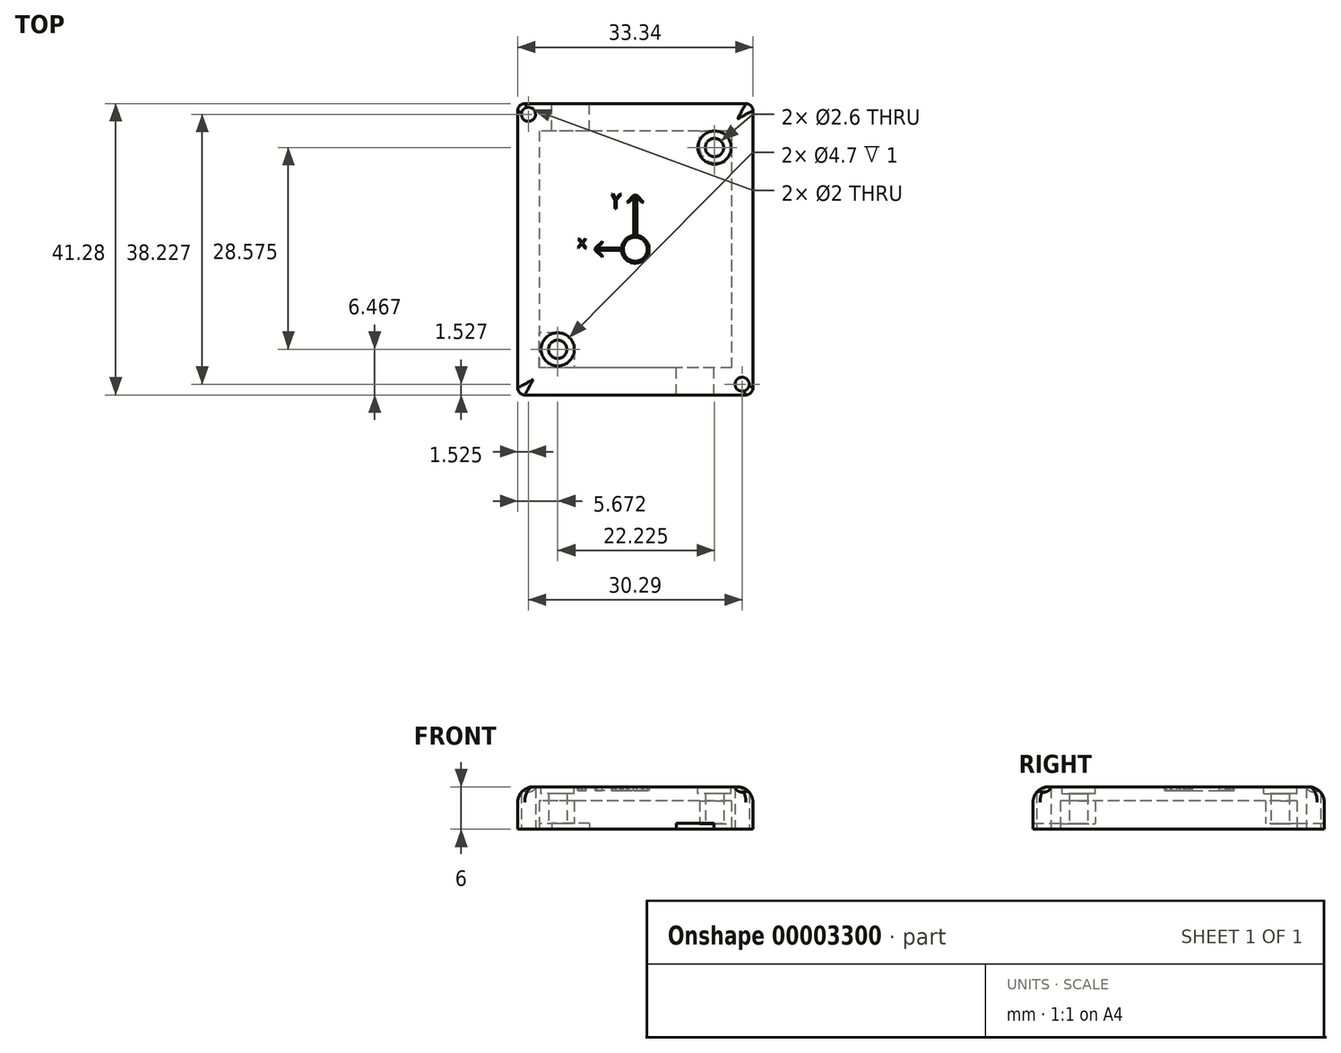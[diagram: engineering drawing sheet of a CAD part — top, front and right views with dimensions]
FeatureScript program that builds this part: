
annotation { "Feature Type Name" : "Feature", "Feature Type Description" : "" }
export const myFeature = defineFeature(function(context is Context, id is Id, definition is map)
    precondition{}
    {
        {
            var Q0;
            Q0=qCreatedBy(makeId("Top.planeOp"),FACE);
            var sketch = newSketch(context, id + "F0", { "sketchPlane" : qUnion([Q0])});
            skLineSegment(sketch, "E0.rect.bottom", {"start": v(16.67, 20.64) * mm, "end": v(-16.67, 20.64) * mm});
            skLineSegment(sketch, "E0.rect.top", {"start": v(16.67, -20.64) * mm, "end": v(-16.67, -20.64) * mm});
            skLineSegment(sketch, "E0.rect.left", {"start": v(16.67, 20.64) * mm, "end": v(16.67, -20.64) * mm});
            skLineSegment(sketch, "E0.rect.right", {"start": v(-16.67, 20.64) * mm, "end": v(-16.67, -20.64) * mm});
            skPoint(sketch, "E0.rect.middle", {"position": v(0, 0) * mm});
            skSolve(sketch);
        }
        {
            var Q0;
            Q0=makeQuery(id+"F0.imprint","IMPRINT",FACE,{"disambiguationData":[TD([[makeQuery(id+"F0.imprint","IMPRINT",EDGE,{"derivedFrom":sQuery(id+"F0.wireOp",EDGE,"E0.rect.bottom")}),1.0]])]});
            extrude(context, id + "F1", {"entities" : qUnion([Q0]), "oppositeDirection" : true, "depth" : 6 * mm});
        }
        {
            var Q0;
            Q0=makeQuery(id+"F1.opExtrude","CAP_FACE",FACE,{"disambiguationData":[OSD([sQuery(id+"F0.wireOp",EDGE,"E0.rect.bottom"),sQuery(id+"F0.wireOp",EDGE,"E0.rect.top"),sQuery(id+"F0.wireOp",EDGE,"E0.rect.left"),sQuery(id+"F0.wireOp",EDGE,"E0.rect.right")])],"isStart":true});
            var sketch = newSketch(context, id + "F2", { "sketchPlane" : qUnion([Q0])});
            skLineSegment(sketch, "E1.rect.bottom", {"start": v(13.33, 16.51) * mm, "end": v(-13.34, 16.51) * mm});
            skLineSegment(sketch, "E1.rect.top", {"start": v(13.34, -16.51) * mm, "end": v(-13.33, -16.51) * mm});
            skLineSegment(sketch, "E1.rect.left", {"start": v(13.33, 16.51) * mm, "end": v(13.34, -16.51) * mm});
            skLineSegment(sketch, "E1.rect.right", {"start": v(-13.34, 16.51) * mm, "end": v(-13.33, -16.51) * mm});
            skPoint(sketch, "E1.rect.middle", {"position": v(0, 0) * mm});
            skCircle(sketch, "E2", {"center": v(11.23, 14.4) * mm, "radius": 1.25 * mm});
            skCircle(sketch, "E3", {"center": v(-11, -14.17) * mm, "radius": 1.25 * mm});
            skCircle(sketch, "E4", {"center": v(11.23, 14.4) * mm, "radius": 2.1 * mm});
            skCircle(sketch, "E5", {"center": v(-11, -14.17) * mm, "radius": 2.34 * mm});
            skLineSegment(sketch, "E6.0", {"start": v(13.59, 16.76) * mm, "end": v(-13.59, 16.76) * mm});
            skLineSegment(sketch, "E6.1", {"start": v(13.59, 16.76) * mm, "end": v(13.59, -16.76) * mm});
            skLineSegment(sketch, "E6.2", {"start": v(13.59, -16.76) * mm, "end": v(-13.59, -16.76) * mm});
            skLineSegment(sketch, "E6.3", {"start": v(-13.59, 16.76) * mm, "end": v(-13.59, -16.76) * mm});
            skLineSegment(sketch, "E7", {"start": v(9.12, 14.4) * mm, "end": v(9.12, 16.76) * mm});
            skLineSegment(sketch, "E8", {"start": v(11.23, 12.3) * mm, "end": v(13.59, 12.3) * mm});
            skLineSegment(sketch, "E9", {"start": v(-11, -11.84) * mm, "end": v(-13.59, -11.84) * mm});
            skLineSegment(sketch, "E10", {"start": v(-8.66, -14.17) * mm, "end": v(-8.66, -16.76) * mm});
            skSolve(sketch);
        }
        {
            var Q0;
            {var subQ6=sQuery(id+"F2.wireOp",EDGE,"E1.rect.right");var subQ10=sQuery(id+"F2.wireOp",EDGE,"E1.rect.bottom");var subQ18=makeQuery(id+"F2.imprint","INTERSECT",VERTEX,{"derivedFrom":[subQ10,subQ6]});Q0=makeQuery(id+"F2.imprint","IMPRINT",FACE,{"disambiguationData":[TD([[makeQuery(id+"F2.imprint","IMPRINT",EDGE,{"disambiguationData":[TD([[subQ18,1.0]])],"derivedFrom":subQ10}),1.0]])]});}
            var Q1;
            {var subQ1=sQuery(id+"F2.wireOp",EDGE,"E1.rect.right");var subQ6=sQuery(id+"F2.wireOp",EDGE,"E1.rect.bottom");var subQ11=makeQuery(id+"F2.imprint","INTERSECT",VERTEX,{"derivedFrom":[subQ6,subQ1]});Q1=makeQuery(id+"F2.imprint","IMPRINT",FACE,{"disambiguationData":[TD([[makeQuery(id+"F2.imprint","IMPRINT",EDGE,{"disambiguationData":[TD([[subQ11,1.0]])],"derivedFrom":subQ6}),-1.0]])]});}
            var Q2;
            {var subQ1=sQuery(id+"F2.wireOp",EDGE,"E1.rect.left");var subQ6=sQuery(id+"F2.wireOp",EDGE,"E1.rect.top");var subQ11=makeQuery(id+"F2.imprint","INTERSECT",VERTEX,{"derivedFrom":[subQ6,subQ1]});Q2=makeQuery(id+"F2.imprint","IMPRINT",FACE,{"disambiguationData":[TD([[makeQuery(id+"F2.imprint","IMPRINT",EDGE,{"disambiguationData":[TD([[subQ11,-1.0]])],"derivedFrom":subQ6}),1.0]])]});}
            extrude(context, id + "F3", {"entities" : qUnion([Q0, Q1, Q2]), "operationType" : NewBodyOperationType.REMOVE, "oppositeDirection" : true, "depth" : 4 * mm});
        }
        {
            var Q0;
            Q0=makeQuery(id+"F1.opExtrude","CAP_FACE",FACE,{"disambiguationData":[OSD([sQuery(id+"F0.wireOp",EDGE,"E0.rect.bottom"),sQuery(id+"F0.wireOp",EDGE,"E0.rect.top"),sQuery(id+"F0.wireOp",EDGE,"E0.rect.left"),sQuery(id+"F0.wireOp",EDGE,"E0.rect.right")])],"isStart":true});
            var sketch = newSketch(context, id + "F4", { "sketchPlane" : qUnion([Q0])});
            skLineSegment(sketch, "E11", {"start": v(9.12, 16.76) * mm, "end": v(13.59, 16.76) * mm});
            skLineSegment(sketch, "E12", {"start": v(13.59, 16.76) * mm, "end": v(13.59, 12.3) * mm});
            skLineSegment(sketch, "E13", {"start": v(13.59, 12.3) * mm, "end": v(11.23, 12.3) * mm});
            skArc(sketch, "E14", {"start": v(9.12, 14.4) * mm, "mid": v(9.74, 12.91) * mm, "end": v(11.23, 12.3) * mm});
            skLineSegment(sketch, "E15", {"start": v(9.12, 14.4) * mm, "end": v(9.12, 16.76) * mm});
            skArc(sketch, "E16", {"start": v(-8.66, -14.17) * mm, "mid": v(-9.35, -12.52) * mm, "end": v(-11, -11.84) * mm});
            skLineSegment(sketch, "E17", {"start": v(-8.66, -14.17) * mm, "end": v(-8.66, -16.76) * mm});
            skLineSegment(sketch, "E18", {"start": v(-8.66, -16.76) * mm, "end": v(-13.59, -16.76) * mm});
            skLineSegment(sketch, "E19", {"start": v(-13.59, -16.76) * mm, "end": v(-13.59, -11.84) * mm});
            skLineSegment(sketch, "E20", {"start": v(-13.59, -11.84) * mm, "end": v(-11, -11.84) * mm});
            skSolve(sketch);
        }
        {
            var Q0;
            {Q0=qUnion([makeQuery(id+"F4.imprint","IMPRINT",FACE,{"disambiguationData":[TD([[makeQuery(id+"F4.imprint","IMPRINT",EDGE,{"derivedFrom":sQuery(id+"F4.wireOp",EDGE,"E11")}),-1.0]])]}),makeQuery(id+"F4.imprint","IMPRINT",FACE,{"disambiguationData":[TD([[makeQuery(id+"F4.imprint","IMPRINT",EDGE,{"derivedFrom":sQuery(id+"F4.wireOp",EDGE,"E16")}),1.0]])]})]);}
            extrude(context, id + "F5", {"entities" : qUnion([Q0]), "operationType" : NewBodyOperationType.REMOVE, "oppositeDirection" : true, "depth" : .8 * mm});
        }
        {
            var Q0;
            Q0=makeQuery(id+"F5.boolean.opBoolean","COPY",FACE,{"derivedFrom":makeQuery(id+"F5.opExtrude","CAP_FACE",FACE,{"disambiguationData":[OSD([sQuery(id+"F4.wireOp",EDGE,"E11"),sQuery(id+"F4.wireOp",EDGE,"E12"),sQuery(id+"F4.wireOp",EDGE,"E13"),sQuery(id+"F4.wireOp",EDGE,"E14"),sQuery(id+"F4.wireOp",EDGE,"E15")])],"isStart":false})});
            var sketch = newSketch(context, id + "F6", { "sketchPlane" : qUnion([Q0])});
            skCircle(sketch, "E21", {"center": v(11.23, 14.4) * mm, "radius": 1.3 * mm});
            skSolve(sketch);
        }
        {
            var Q0;
            Q0=makeQuery(id+"F6.imprint","IMPRINT",FACE,{"disambiguationData":[TD([[makeQuery(id+"F6.imprint","IMPRINT",EDGE,{"derivedFrom":sQuery(id+"F6.wireOp",EDGE,"E21")}),1.0]])]});
            extrude(context, id + "F7", {"entities" : qUnion([Q0]), "operationType" : NewBodyOperationType.REMOVE, "oppositeDirection" : true, "depth" : 25.4 * mm});
        }
        {
            var Q0;
            Q0=makeQuery(id+"F5.boolean.opBoolean","COPY",FACE,{"derivedFrom":makeQuery(id+"F5.opExtrude","CAP_FACE",FACE,{"disambiguationData":[OSD([sQuery(id+"F4.wireOp",EDGE,"E16"),sQuery(id+"F4.wireOp",EDGE,"E17"),sQuery(id+"F4.wireOp",EDGE,"E18"),sQuery(id+"F4.wireOp",EDGE,"E19"),sQuery(id+"F4.wireOp",EDGE,"E20")])],"isStart":false})});
            var sketch = newSketch(context, id + "F8", { "sketchPlane" : qUnion([Q0])});
            skCircle(sketch, "E22", {"center": v(-11, -14.17) * mm, "radius": 1.3 * mm});
            skSolve(sketch);
        }
        {
            var Q0;
            Q0=makeQuery(id+"F8.imprint","IMPRINT",FACE,{"disambiguationData":[TD([[makeQuery(id+"F8.imprint","IMPRINT",EDGE,{"derivedFrom":sQuery(id+"F8.wireOp",EDGE,"E22")}),1.0]])]});
            extrude(context, id + "F9", {"entities" : qUnion([Q0]), "operationType" : NewBodyOperationType.REMOVE, "oppositeDirection" : true, "depth" : 25.4 * mm});
        }
        {
            var Q0;
            Q0=makeQuery(id+"F1.opExtrude","CAP_FACE",FACE,{"disambiguationData":[OSD([sQuery(id+"F0.wireOp",EDGE,"E0.rect.bottom"),sQuery(id+"F0.wireOp",EDGE,"E0.rect.top"),sQuery(id+"F0.wireOp",EDGE,"E0.rect.left"),sQuery(id+"F0.wireOp",EDGE,"E0.rect.right")])],"isStart":true});
            var sketch = newSketch(context, id + "F10", { "sketchPlane" : qUnion([Q0])});
            skLineSegment(sketch, "E23.bottom", {"start": v(-13.59, 16.76) * mm, "end": v(-5.09, 16.76) * mm});
            skLineSegment(sketch, "E23.top", {"start": v(-13.59, 20.64) * mm, "end": v(-5.09, 20.64) * mm});
            skLineSegment(sketch, "E23.left", {"start": v(-13.59, 16.76) * mm, "end": v(-13.59, 20.64) * mm});
            skLineSegment(sketch, "E23.right", {"start": v(-5.09, 16.76) * mm, "end": v(-5.09, 20.64) * mm});
            skLineSegment(sketch, "E24.bottom", {"start": v(13.59, -16.76) * mm, "end": v(4.59, -16.76) * mm});
            skLineSegment(sketch, "E24.top", {"start": v(13.59, -20.64) * mm, "end": v(4.59, -20.64) * mm});
            skLineSegment(sketch, "E24.left", {"start": v(13.59, -16.76) * mm, "end": v(13.59, -20.64) * mm});
            skLineSegment(sketch, "E24.right", {"start": v(4.59, -16.76) * mm, "end": v(4.59, -20.64) * mm});
            skSolve(sketch);
        }
        {
            var Q0;
            {Q0=qUnion([makeQuery(id+"F10.imprint","IMPRINT",FACE,{"disambiguationData":[TD([[makeQuery(id+"F10.imprint","IMPRINT",EDGE,{"derivedFrom":sQuery(id+"F10.wireOp",EDGE,"E23.bottom")}),-1.0]])]}),makeQuery(id+"F10.imprint","IMPRINT",FACE,{"disambiguationData":[TD([[makeQuery(id+"F10.imprint","IMPRINT",EDGE,{"derivedFrom":sQuery(id+"F10.wireOp",EDGE,"E24.bottom")}),1.0]])]})]);}
            extrude(context, id + "F11", {"entities" : qUnion([Q0]), "operationType" : NewBodyOperationType.REMOVE, "oppositeDirection" : true, "depth" : .4 * mm});
        }
        {
            var Q0;
            Q0=makeQuery(id+"F1.opExtrude","SWEPT_BODY",BODY,{"disambiguationData":[OSD([sQuery(id+"F0.wireOp",EDGE,"E0.rect.bottom"),sQuery(id+"F0.wireOp",EDGE,"E0.rect.top"),sQuery(id+"F0.wireOp",EDGE,"E0.rect.left"),sQuery(id+"F0.wireOp",EDGE,"E0.rect.right")])]});
            var Q1;
            Q1=qCreatedBy(makeId("Top.planeOp"),FACE);
            mirror(context, id + "F12", {"entities" : qUnion([Q0]), "mirrorPlane" : qUnion([Q1])});
        }
        {
            var Q0;
            Q0=makeQuery(id+"F1.opExtrude","SWEPT_BODY",BODY,{"disambiguationData":[OSD([sQuery(id+"F0.wireOp",EDGE,"E0.rect.bottom"),sQuery(id+"F0.wireOp",EDGE,"E0.rect.top"),sQuery(id+"F0.wireOp",EDGE,"E0.rect.left"),sQuery(id+"F0.wireOp",EDGE,"E0.rect.right")])]});
            deleteBodies(context, id + "F13", {"entities" : qUnion([Q0])});
        }
        {
            var Q0;
            Q0=makeQuery(id+"F12.opPattern","COPY",FACE,{"derivedFrom":makeQuery(id+"F1.opExtrude","CAP_FACE",FACE,{"disambiguationData":[OSD([sQuery(id+"F0.wireOp",EDGE,"E0.rect.bottom"),sQuery(id+"F0.wireOp",EDGE,"E0.rect.top"),sQuery(id+"F0.wireOp",EDGE,"E0.rect.left"),sQuery(id+"F0.wireOp",EDGE,"E0.rect.right")])],"isStart":false}),"instanceName":"1"});
            var sketch = newSketch(context, id + "F14", { "sketchPlane" : qUnion([Q0])});
            skCircle(sketch, "E25", {"center": v(11.23, 14.4) * mm, "radius": 2.35 * mm});
            skCircle(sketch, "E26", {"center": v(-11, -14.17) * mm, "radius": 2.35 * mm});
            skSolve(sketch);
        }
        {
            var Q0;
            {var subQ0=makeQuery(id+"F1.opExtrude","CAP_FACE",FACE,{"disambiguationData":[OSD([sQuery(id+"F0.wireOp",EDGE,"E0.rect.bottom"),sQuery(id+"F0.wireOp",EDGE,"E0.rect.top"),sQuery(id+"F0.wireOp",EDGE,"E0.rect.left"),sQuery(id+"F0.wireOp",EDGE,"E0.rect.right")])],"isStart":false});var subQ1=makeQuery(id+"F14.imprint","IMPRINT",EDGE,{"derivedFrom":makeQuery(id+"F12.opPattern","COPY",EDGE,{"derivedFrom":makeQuery(id+"F7.boolean.opBoolean","INTERSECT",EDGE,{"derivedFrom":[subQ0,makeQuery(id+"F7.opExtrude","SWEPT_FACE",FACE,{"disambiguationData":[OSD([sQuery(id+"F6.wireOp",EDGE,"E21")])]})]}),"instanceName":"1"})});var subQ2=makeQuery(id+"F14.imprint","IMPRINT",EDGE,{"derivedFrom":makeQuery(id+"F12.opPattern","COPY",EDGE,{"derivedFrom":makeQuery(id+"F9.boolean.opBoolean","INTERSECT",EDGE,{"derivedFrom":[subQ0,makeQuery(id+"F9.opExtrude","SWEPT_FACE",FACE,{"disambiguationData":[OSD([sQuery(id+"F8.wireOp",EDGE,"E22")])]})]}),"instanceName":"1"})});Q0=qUnion([makeQuery(id+"F14.imprint","IMPRINT",FACE,{"disambiguationData":[TD([[subQ1,1.0]])]}),makeQuery(id+"F14.imprint","IMPRINT",FACE,{"disambiguationData":[TD([[subQ2,1.0]])]}),makeQuery(id+"F14.imprint","IMPRINT",FACE,{"disambiguationData":[TD([[makeQuery(id+"F14.imprint","IMPRINT",EDGE,{"derivedFrom":sQuery(id+"F14.wireOp",EDGE,"E25")}),1.0]])]}),makeQuery(id+"F14.imprint","IMPRINT",FACE,{"disambiguationData":[TD([[makeQuery(id+"F14.imprint","IMPRINT",EDGE,{"derivedFrom":sQuery(id+"F14.wireOp",EDGE,"E26")}),1.0]])]})]);}
            extrude(context, id + "F15", {"entities" : qUnion([Q0]), "operationType" : NewBodyOperationType.REMOVE, "oppositeDirection" : true, "depth" : 1 * mm});
        }
        {
            var Q0;
            {var subQ0=sQuery(id+"F0.wireOp",EDGE,"E0.rect.bottom");var subQ1=sQuery(id+"F0.wireOp",EDGE,"E0.rect.top");var subQ2=sQuery(id+"F0.wireOp",EDGE,"E0.rect.right");Q0=makeQuery(id+"F12.opPattern","COPY",FACE,{"derivedFrom":makeQuery(id+"F11.boolean.opBoolean","SPLIT",FACE,{"disambiguationData":[TD([makeQuery(id+"F1.opExtrude","SWEPT_FACE",FACE,{"disambiguationData":[OSD([subQ2])]})])],"derivedFrom":makeQuery(id+"F1.opExtrude","CAP_FACE",FACE,{"disambiguationData":[OSD([subQ0,subQ1,sQuery(id+"F0.wireOp",EDGE,"E0.rect.left"),subQ2])],"isStart":true})}),"instanceName":"1"});}
            var sketch = newSketch(context, id + "F16", { "sketchPlane" : qUnion([Q0])});
            skCircle(sketch, "E27", {"center": v(-15.14, -19.11) * mm, "radius": 1 * mm});
            skSolve(sketch);
        }
        {
            var Q0;
            Q0=makeQuery(id+"F16.imprint","IMPRINT",FACE,{"disambiguationData":[TD([[makeQuery(id+"F16.imprint","IMPRINT",EDGE,{"derivedFrom":sQuery(id+"F16.wireOp",EDGE,"E27")}),1.0]])]});
            extrude(context, id + "F17", {"entities" : qUnion([Q0]), "operationType" : NewBodyOperationType.REMOVE, "oppositeDirection" : true, "depth" : 20 * mm});
        }
        {
            var Q0;
            {var subQ0=sQuery(id+"F0.wireOp",EDGE,"E0.rect.bottom");var subQ1=sQuery(id+"F0.wireOp",EDGE,"E0.rect.top");var subQ2=sQuery(id+"F0.wireOp",EDGE,"E0.rect.left");Q0=makeQuery(id+"F12.opPattern","COPY",FACE,{"derivedFrom":makeQuery(id+"F11.boolean.opBoolean","SPLIT",FACE,{"disambiguationData":[TD([makeQuery(id+"F1.opExtrude","SWEPT_FACE",FACE,{"disambiguationData":[OSD([subQ2])]})])],"derivedFrom":makeQuery(id+"F1.opExtrude","CAP_FACE",FACE,{"disambiguationData":[OSD([subQ0,subQ1,subQ2,sQuery(id+"F0.wireOp",EDGE,"E0.rect.right")])],"isStart":true})}),"instanceName":"1"});}
            var sketch = newSketch(context, id + "F18", { "sketchPlane" : qUnion([Q0])});
            skCircle(sketch, "E28", {"center": v(15.14, 19.11) * mm, "radius": 1 * mm});
            skSolve(sketch);
        }
        {
            var Q0;
            Q0=makeQuery(id+"F18.imprint","IMPRINT",FACE,{"disambiguationData":[TD([[makeQuery(id+"F18.imprint","IMPRINT",EDGE,{"derivedFrom":sQuery(id+"F18.wireOp",EDGE,"E28")}),1.0]])]});
            extrude(context, id + "F19", {"entities" : qUnion([Q0]), "operationType" : NewBodyOperationType.REMOVE, "oppositeDirection" : true, "depth" : 25 * mm});
        }
        {
            var Q0;
            Q0=makeQuery(id+"F12.opPattern","COPY",EDGE,{"derivedFrom":makeQuery(id+"F1.opExtrude","CAP_EDGE",EDGE,{"disambiguationData":[OSD([sQuery(id+"F0.wireOp",EDGE,"E0.rect.top")])],"isStart":false}),"instanceName":"1"});
            var Q1;
            Q1=makeQuery(id+"F12.opPattern","COPY",EDGE,{"derivedFrom":makeQuery(id+"F1.opExtrude","CAP_EDGE",EDGE,{"disambiguationData":[OSD([sQuery(id+"F0.wireOp",EDGE,"E0.rect.left")])],"isStart":false}),"instanceName":"1"});
            var Q2;
            Q2=makeQuery(id+"F12.opPattern","COPY",EDGE,{"derivedFrom":makeQuery(id+"F1.opExtrude","CAP_EDGE",EDGE,{"disambiguationData":[OSD([sQuery(id+"F0.wireOp",EDGE,"E0.rect.bottom")])],"isStart":false}),"instanceName":"1"});
            var Q3;
            Q3=makeQuery(id+"F12.opPattern","COPY",EDGE,{"derivedFrom":makeQuery(id+"F1.opExtrude","CAP_EDGE",EDGE,{"disambiguationData":[OSD([sQuery(id+"F0.wireOp",EDGE,"E0.rect.right")])],"isStart":false}),"instanceName":"1"});
            fillet(context, id + "F20", {"entities" : qUnion([Q0, Q1, Q2, Q3]), "radius" : 2.2 * mm, "tangentPropagation" : true, "allowEdgeOverflow" : false});
        }
        {
            var Q0;
            Q0=makeQuery(id+"F12.opPattern","COPY",EDGE,{"derivedFrom":makeQuery(id+"F1.opExtrude","SWEPT_EDGE",EDGE,{"disambiguationData":[OSD([sQuery(id+"F0.wireOp",EDGE,"E0.rect.bottom"),sQuery(id+"F0.wireOp",EDGE,"E0.rect.right")])]}),"instanceName":"1"});
            var Q1;
            Q1=makeQuery(id+"F12.opPattern","COPY",EDGE,{"derivedFrom":makeQuery(id+"F1.opExtrude","SWEPT_EDGE",EDGE,{"disambiguationData":[OSD([sQuery(id+"F0.wireOp",EDGE,"E0.rect.bottom"),sQuery(id+"F0.wireOp",EDGE,"E0.rect.left")])]}),"instanceName":"1"});
            var Q2;
            Q2=makeQuery(id+"F12.opPattern","COPY",EDGE,{"derivedFrom":makeQuery(id+"F1.opExtrude","SWEPT_EDGE",EDGE,{"disambiguationData":[OSD([sQuery(id+"F0.wireOp",EDGE,"E0.rect.top"),sQuery(id+"F0.wireOp",EDGE,"E0.rect.right")])]}),"instanceName":"1"});
            var Q3;
            Q3=makeQuery(id+"F12.opPattern","COPY",EDGE,{"derivedFrom":makeQuery(id+"F1.opExtrude","SWEPT_EDGE",EDGE,{"disambiguationData":[OSD([sQuery(id+"F0.wireOp",EDGE,"E0.rect.top"),sQuery(id+"F0.wireOp",EDGE,"E0.rect.left")])]}),"instanceName":"1"});
            fillet(context, id + "F21", {"entities" : qUnion([Q0, Q1, Q2, Q3]), "radius" : 1 * mm, "tangentPropagation" : true, "allowEdgeOverflow" : false});
        }
        {
            var Q0;
            Q0=makeQuery(id+"F12.opPattern","COPY",FACE,{"derivedFrom":makeQuery(id+"F1.opExtrude","CAP_FACE",FACE,{"disambiguationData":[OSD([sQuery(id+"F0.wireOp",EDGE,"E0.rect.bottom"),sQuery(id+"F0.wireOp",EDGE,"E0.rect.top"),sQuery(id+"F0.wireOp",EDGE,"E0.rect.left"),sQuery(id+"F0.wireOp",EDGE,"E0.rect.right")])],"isStart":false}),"instanceName":"1"});
            var sketch = newSketch(context, id + "F22", { "sketchPlane" : qUnion([Q0])});
            skCircle(sketch, "E29", {"center": v(0, 0) * mm, "radius": 1.7 * mm});
            skLineSegment(sketch, "E30", {"start": v(0, 1.7) * mm, "end": v(0, 7.65) * mm});
            skLineSegment(sketch, "E31", {"start": v(0, 7.65) * mm, "end": v(-0.93, 6.66) * mm});
            skLineSegment(sketch, "E32.0.MirrorCS", {"start": v(0, 7.65) * mm, "end": v(0.93, 6.66) * mm});
            skLineSegment(sketch, "E33", {"start": v(-1.7, 0) * mm, "end": v(-5.65, 0) * mm});
            skLineSegment(sketch, "E34", {"start": v(-5.65, 0) * mm, "end": v(-4.66, -0.93) * mm});
            skLineSegment(sketch, "E35.0.MirrorCS", {"start": v(-5.65, 0) * mm, "end": v(-4.66, 0.93) * mm});
            skLineSegment(sketch, "E36", {"start": v(0, 0) * mm, "end": v(-1.2, 1.2) * mm});
            skLineSegment(sketch, "E37", {"start": v(0, 0) * mm, "end": v(1.2, 1.2) * mm});
            skLineSegment(sketch, "E38", {"start": v(0, 0) * mm, "end": v(-1.2, -1.2) * mm});
            skLineSegment(sketch, "E39", {"start": v(0, 0) * mm, "end": v(1.2, -1.2) * mm});
            skCircle(sketch, "E40", {"center": v(0, 0) * mm, "radius": 1.97 * mm});
            skLineSegment(sketch, "E41.rect.bottom", {"start": v(-0.24, 1.69) * mm, "end": v(0.24, 1.69) * mm});
            skLineSegment(sketch, "E41.rect.top", {"start": v(-0.24, 7.67) * mm, "end": v(0.24, 7.67) * mm});
            skLineSegment(sketch, "E41.rect.left", {"start": v(-0.24, 1.69) * mm, "end": v(-0.24, 7.67) * mm});
            skLineSegment(sketch, "E41.rect.right", {"start": v(0.24, 1.69) * mm, "end": v(0.24, 7.67) * mm});
            skPoint(sketch, "E41.rect.middle", {"position": v(0, 4.68) * mm});
            skLineSegment(sketch, "E42", {"start": v(-0.24, 7.67) * mm, "end": v(-1.2, 6.66) * mm});
            skLineSegment(sketch, "E43", {"start": v(-1.2, 6.66) * mm, "end": v(-0.93, 6.66) * mm});
            skLineSegment(sketch, "E44", {"start": v(0.24, 7.67) * mm, "end": v(1.2, 6.66) * mm});
            skLineSegment(sketch, "E45", {"start": v(1.2, 6.66) * mm, "end": v(0.93, 6.66) * mm});
            skLineSegment(sketch, "E46.rect.bottom", {"start": v(-1.7, -0.18) * mm, "end": v(-5.66, -0.18) * mm});
            skLineSegment(sketch, "E46.rect.top", {"start": v(-1.7, 0.18) * mm, "end": v(-5.66, 0.18) * mm});
            skLineSegment(sketch, "E46.rect.left", {"start": v(-1.7, -0.18) * mm, "end": v(-1.7, 0.18) * mm});
            skLineSegment(sketch, "E46.rect.right", {"start": v(-5.66, -0.18) * mm, "end": v(-5.66, 0.18) * mm});
            skPoint(sketch, "E46.rect.middle", {"position": v(-3.68, 0) * mm});
            skLineSegment(sketch, "E47", {"start": v(-5.66, 0.18) * mm, "end": v(-4.66, 1.12) * mm});
            skLineSegment(sketch, "E48", {"start": v(-4.66, 1.12) * mm, "end": v(-4.66, 0.93) * mm});
            skLineSegment(sketch, "E49", {"start": v(-5.66, -0.18) * mm, "end": v(-4.66, -1.12) * mm});
            skLineSegment(sketch, "E50", {"start": v(-4.66, -1.12) * mm, "end": v(-4.66, -0.93) * mm});
            skLineSegment(sketch, "E51", {"start": v(-8.1, 1.43) * mm, "end": v(-7.1, 0.12) * mm});
            skLineSegment(sketch, "E52", {"start": v(-7.01, 1.4) * mm, "end": v(-8.09, 0.18) * mm});
            skLineSegment(sketch, "E53", {"start": v(-8.09, 0.18) * mm, "end": v(-8.18, 0.26) * mm});
            skLineSegment(sketch, "E54", {"start": v(-8.18, 0.26) * mm, "end": v(-7.1, 1.48) * mm});
            skLineSegment(sketch, "E55", {"start": v(-7.1, 1.48) * mm, "end": v(-7.01, 1.4) * mm});
            skLineSegment(sketch, "E56", {"start": v(-8.1, 1.43) * mm, "end": v(-7.98, 1.52) * mm});
            skLineSegment(sketch, "E57", {"start": v(-7.98, 1.52) * mm, "end": v(-6.97, 0.2) * mm});
            skLineSegment(sketch, "E58", {"start": v(-6.97, 0.2) * mm, "end": v(-7.1, 0.12) * mm});
            skLineSegment(sketch, "E59", {"start": v(-2.86, 6.93) * mm, "end": v(-2.86, 5.77) * mm});
            skLineSegment(sketch, "E60", {"start": v(-2.86, 5.77) * mm, "end": v(-2.7, 5.77) * mm});
            skLineSegment(sketch, "E61", {"start": v(-2.7, 5.77) * mm, "end": v(-2.7, 6.95) * mm});
            skLineSegment(sketch, "E62", {"start": v(-2.7, 6.95) * mm, "end": v(-2.03, 7.8) * mm});
            skLineSegment(sketch, "E63", {"start": v(-2.03, 7.8) * mm, "end": v(-2.14, 7.88) * mm});
            skLineSegment(sketch, "E64", {"start": v(-2.14, 7.88) * mm, "end": v(-2.74, 7.12) * mm});
            skLineSegment(sketch, "E65", {"start": v(-2.74, 7.12) * mm, "end": v(-3.19, 7.85) * mm});
            skLineSegment(sketch, "E66", {"start": v(-3.19, 7.85) * mm, "end": v(-3.32, 7.77) * mm});
            skLineSegment(sketch, "E67", {"start": v(-3.32, 7.77) * mm, "end": v(-2.86, 6.93) * mm});
            skSolve(sketch);
        }
        {
            var Q0;
            {var subQ3=sQuery(id+"F22.wireOp",EDGE,"E29");var subQ10=makeQuery(id+"F22.imprint","INTERSECT",VERTEX,{"derivedFrom":[subQ3,sQuery(id+"F22.wireOp",EDGE,"E38")]});Q0=makeQuery(id+"F22.imprint","IMPRINT",FACE,{"disambiguationData":[TD([[makeQuery(id+"F22.imprint","IMPRINT",EDGE,{"disambiguationData":[TD([[subQ10,-1.0]])],"derivedFrom":subQ3}),-1.0]])]});}
            var Q1;
            {var subQ1=sQuery(id+"F22.wireOp",EDGE,"E40");var subQ5=sQuery(id+"F22.wireOp",EDGE,"E41.rect.left");var subQ6=makeQuery(id+"F22.imprint","INTERSECT",VERTEX,{"derivedFrom":[subQ1,subQ5]});Q1=makeQuery(id+"F22.imprint","IMPRINT",FACE,{"disambiguationData":[TD([[makeQuery(id+"F22.imprint","IMPRINT",EDGE,{"disambiguationData":[TD([[subQ6,-1.0]])],"derivedFrom":subQ1}),1.0]])]});}
            var Q2;
            {var subQ3=sQuery(id+"F22.wireOp",EDGE,"E29");var subQ5=sQuery(id+"F22.wireOp",EDGE,"E30");var subQ7=makeQuery(id+"F22.imprint","INTERSECT",VERTEX,{"derivedFrom":[subQ3,subQ5]});Q2=makeQuery(id+"F22.imprint","IMPRINT",FACE,{"disambiguationData":[TD([[makeQuery(id+"F22.imprint","IMPRINT",EDGE,{"disambiguationData":[TD([[subQ7,-1.0]])],"derivedFrom":subQ5}),1.0]])]});}
            var Q3;
            {var subQ3=sQuery(id+"F22.wireOp",EDGE,"E29");var subQ5=sQuery(id+"F22.wireOp",EDGE,"E30");var subQ7=makeQuery(id+"F22.imprint","INTERSECT",VERTEX,{"derivedFrom":[subQ3,subQ5]});Q3=makeQuery(id+"F22.imprint","IMPRINT",FACE,{"disambiguationData":[TD([[makeQuery(id+"F22.imprint","IMPRINT",EDGE,{"disambiguationData":[TD([[subQ7,-1.0]])],"derivedFrom":subQ5}),-1.0]])]});}
            var Q4;
            {var subQ1=sQuery(id+"F22.wireOp",EDGE,"E40");var subQ5=sQuery(id+"F22.wireOp",EDGE,"E30");var subQ6=makeQuery(id+"F22.imprint","INTERSECT",VERTEX,{"derivedFrom":[subQ5,subQ1]});Q4=makeQuery(id+"F22.imprint","IMPRINT",FACE,{"disambiguationData":[TD([[makeQuery(id+"F22.imprint","IMPRINT",EDGE,{"disambiguationData":[TD([[subQ6,-1.0]])],"derivedFrom":subQ1}),-1.0]])]});}
            var Q5;
            {var subQ1=sQuery(id+"F22.wireOp",EDGE,"E40");var subQ5=sQuery(id+"F22.wireOp",EDGE,"E30");var subQ6=makeQuery(id+"F22.imprint","INTERSECT",VERTEX,{"derivedFrom":[subQ5,subQ1]});Q5=makeQuery(id+"F22.imprint","IMPRINT",FACE,{"disambiguationData":[TD([[makeQuery(id+"F22.imprint","IMPRINT",EDGE,{"disambiguationData":[TD([[subQ6,1.0]])],"derivedFrom":subQ1}),-1.0]])]});}
            var Q6;
            {var subQ1=sQuery(id+"F22.wireOp",EDGE,"E40");var subQ5=sQuery(id+"F22.wireOp",EDGE,"E33");var subQ6=makeQuery(id+"F22.imprint","INTERSECT",VERTEX,{"derivedFrom":[subQ5,subQ1]});Q6=makeQuery(id+"F22.imprint","IMPRINT",FACE,{"disambiguationData":[TD([[makeQuery(id+"F22.imprint","IMPRINT",EDGE,{"disambiguationData":[TD([[subQ6,1.0]])],"derivedFrom":subQ1}),-1.0]])]});}
            var Q7;
            {var subQ1=sQuery(id+"F22.wireOp",EDGE,"E40");var subQ5=sQuery(id+"F22.wireOp",EDGE,"E33");var subQ6=makeQuery(id+"F22.imprint","INTERSECT",VERTEX,{"derivedFrom":[subQ5,subQ1]});Q7=makeQuery(id+"F22.imprint","IMPRINT",FACE,{"disambiguationData":[TD([[makeQuery(id+"F22.imprint","IMPRINT",EDGE,{"disambiguationData":[TD([[subQ6,-1.0]])],"derivedFrom":subQ1}),-1.0]])]});}
            var Q8;
            {var subQ3=sQuery(id+"F22.wireOp",EDGE,"E29");var subQ5=sQuery(id+"F22.wireOp",EDGE,"E33");var subQ7=makeQuery(id+"F22.imprint","INTERSECT",VERTEX,{"derivedFrom":[subQ3,subQ5]});Q8=makeQuery(id+"F22.imprint","IMPRINT",FACE,{"disambiguationData":[TD([[makeQuery(id+"F22.imprint","IMPRINT",EDGE,{"disambiguationData":[TD([[subQ7,-1.0]])],"derivedFrom":subQ5}),1.0]])]});}
            var Q9;
            {var subQ3=sQuery(id+"F22.wireOp",EDGE,"E29");var subQ5=sQuery(id+"F22.wireOp",EDGE,"E33");var subQ7=makeQuery(id+"F22.imprint","INTERSECT",VERTEX,{"derivedFrom":[subQ3,subQ5]});Q9=makeQuery(id+"F22.imprint","IMPRINT",FACE,{"disambiguationData":[TD([[makeQuery(id+"F22.imprint","IMPRINT",EDGE,{"disambiguationData":[TD([[subQ7,-1.0]])],"derivedFrom":subQ5}),-1.0]])]});}
            var Q10;
            {var subQ1=sQuery(id+"F22.wireOp",EDGE,"E49");Q10=makeQuery(id+"F22.imprint","IMPRINT",FACE,{"disambiguationData":[TD([[makeQuery(id+"F22.imprint","IMPRINT",EDGE,{"derivedFrom":subQ1}),1.0]])]});}
            var Q11;
            {var subQ1=sQuery(id+"F22.wireOp",EDGE,"E47");Q11=makeQuery(id+"F22.imprint","IMPRINT",FACE,{"disambiguationData":[TD([[makeQuery(id+"F22.imprint","IMPRINT",EDGE,{"derivedFrom":subQ1}),-1.0]])]});}
            var Q12;
            {var subQ0=sQuery(id+"F22.wireOp",EDGE,"E46.rect.right");Q12=makeQuery(id+"F22.imprint","IMPRINT",FACE,{"disambiguationData":[TD([[makeQuery(id+"F22.imprint","IMPRINT",EDGE,{"derivedFrom":subQ0}),-1.0]])]});}
            var Q13;
            {var subQ1=sQuery(id+"F22.wireOp",EDGE,"E42");Q13=makeQuery(id+"F22.imprint","IMPRINT",FACE,{"disambiguationData":[TD([[makeQuery(id+"F22.imprint","IMPRINT",EDGE,{"derivedFrom":subQ1}),1.0]])]});}
            var Q14;
            {var subQ3=sQuery(id+"F22.wireOp",EDGE,"E41.rect.top");Q14=makeQuery(id+"F22.imprint","IMPRINT",FACE,{"disambiguationData":[TD([[makeQuery(id+"F22.imprint","IMPRINT",EDGE,{"derivedFrom":subQ3}),-1.0]])]});}
            var Q15;
            {var subQ1=sQuery(id+"F22.wireOp",EDGE,"E44");Q15=makeQuery(id+"F22.imprint","IMPRINT",FACE,{"disambiguationData":[TD([[makeQuery(id+"F22.imprint","IMPRINT",EDGE,{"derivedFrom":subQ1}),-1.0]])]});}
            var Q16;
            Q16=makeQuery(id+"F22.imprint","IMPRINT",FACE,{"disambiguationData":[TD([[makeQuery(id+"F22.imprint","IMPRINT",EDGE,{"derivedFrom":sQuery(id+"F22.wireOp",EDGE,"E59")}),1.0]])]});
            var Q17;
            {var subQ5=sQuery(id+"F22.wireOp",EDGE,"E55");Q17=makeQuery(id+"F22.imprint","IMPRINT",FACE,{"disambiguationData":[TD([[makeQuery(id+"F22.imprint","IMPRINT",EDGE,{"derivedFrom":subQ5}),-1.0]])]});}
            var Q18;
            {var subQ1=sQuery(id+"F22.wireOp",EDGE,"E54");var subQ5=sQuery(id+"F22.wireOp",EDGE,"E51");var subQ6=makeQuery(id+"F22.imprint","INTERSECT",VERTEX,{"derivedFrom":[subQ5,subQ1]});Q18=makeQuery(id+"F22.imprint","IMPRINT",FACE,{"disambiguationData":[TD([[makeQuery(id+"F22.imprint","IMPRINT",EDGE,{"disambiguationData":[TD([[subQ6,-1.0]])],"derivedFrom":subQ5}),1.0]])]});}
            var Q19;
            {var subQ3=sQuery(id+"F22.wireOp",EDGE,"E53");Q19=makeQuery(id+"F22.imprint","IMPRINT",FACE,{"disambiguationData":[TD([[makeQuery(id+"F22.imprint","IMPRINT",EDGE,{"derivedFrom":subQ3}),-1.0]])]});}
            var Q20;
            {var subQ0=sQuery(id+"F22.wireOp",EDGE,"E58");Q20=makeQuery(id+"F22.imprint","IMPRINT",FACE,{"disambiguationData":[TD([[makeQuery(id+"F22.imprint","IMPRINT",EDGE,{"derivedFrom":subQ0}),-1.0]])]});}
            var Q21;
            {var subQ3=sQuery(id+"F22.wireOp",EDGE,"E56");Q21=makeQuery(id+"F22.imprint","IMPRINT",FACE,{"disambiguationData":[TD([[makeQuery(id+"F22.imprint","IMPRINT",EDGE,{"derivedFrom":subQ3}),-1.0]])]});}
            extrude(context, id + "F23", {"entities" : qUnion([Q0, Q1, Q2, Q3, Q4, Q5, Q6, Q7, Q8, Q9, Q10, Q11, Q12, Q13, Q14, Q15, Q16, Q17, Q18, Q19, Q20, Q21]), "operationType" : NewBodyOperationType.REMOVE, "oppositeDirection" : true, "depth" : 0.5 * mm});
        }
        {
            var Q0;
            Q0=makeQuery(id+"F12.opPattern","COPY",FACE,{"derivedFrom":makeQuery(id+"F11.boolean.opBoolean","COPY",FACE,{"derivedFrom":makeQuery(id+"F11.opExtrude","CAP_FACE",FACE,{"disambiguationData":[OSD([sQuery(id+"F10.wireOp",EDGE,"E24.bottom"),sQuery(id+"F10.wireOp",EDGE,"E24.top"),sQuery(id+"F10.wireOp",EDGE,"E24.left"),sQuery(id+"F10.wireOp",EDGE,"E24.right")])],"isStart":false})}),"instanceName":"1"});
            var sketch = newSketch(context, id + "F24", { "sketchPlane" : qUnion([Q0])});
            skLineSegment(sketch, "E68.bottom", {"start": v(4.59, 20.64) * mm, "end": v(13.59, 20.64) * mm});
            skLineSegment(sketch, "E68.top", {"start": v(4.59, 16.76) * mm, "end": v(13.59, 16.76) * mm});
            skLineSegment(sketch, "E68.left", {"start": v(4.59, 20.64) * mm, "end": v(4.59, 16.76) * mm});
            skLineSegment(sketch, "E68.right", {"start": v(13.59, 20.64) * mm, "end": v(13.59, 16.76) * mm});
            skSolve(sketch);
        }
        {
            var Q0;
            Q0=makeQuery(id+"F24.imprint","IMPRINT",FACE,{"disambiguationData":[TD([[makeQuery(id+"F24.imprint","IMPRINT",EDGE,{"derivedFrom":sQuery(id+"F24.wireOp",EDGE,"E68.bottom")}),1.0]])]});
            extrude(context, id + "F25", {"entities" : qUnion([Q0]), "operationType" : NewBodyOperationType.ADD, "depth" : .4 * mm});
        }
        {
            var Q0;
            Q0=makeQuery(id+"F12.opPattern","COPY",FACE,{"derivedFrom":makeQuery(id+"F11.boolean.opBoolean","COPY",FACE,{"derivedFrom":makeQuery(id+"F11.opExtrude","CAP_FACE",FACE,{"disambiguationData":[OSD([sQuery(id+"F10.wireOp",EDGE,"E23.bottom"),sQuery(id+"F10.wireOp",EDGE,"E23.top"),sQuery(id+"F10.wireOp",EDGE,"E23.left"),sQuery(id+"F10.wireOp",EDGE,"E23.right")])],"isStart":false})}),"instanceName":"1"});
            var sketch = newSketch(context, id + "F26", { "sketchPlane" : qUnion([Q0])});
            skLineSegment(sketch, "E69.bottom", {"start": v(-5.09, -20.64) * mm, "end": v(-13.59, -20.64) * mm});
            skLineSegment(sketch, "E69.top", {"start": v(-5.09, -16.76) * mm, "end": v(-13.59, -16.76) * mm});
            skLineSegment(sketch, "E69.left", {"start": v(-5.09, -20.64) * mm, "end": v(-5.09, -16.76) * mm});
            skLineSegment(sketch, "E69.right", {"start": v(-13.59, -20.64) * mm, "end": v(-13.59, -16.76) * mm});
            skSolve(sketch);
        }
        {
            var Q0;
            Q0=makeQuery(id+"F26.imprint","IMPRINT",FACE,{"disambiguationData":[TD([[makeQuery(id+"F26.imprint","IMPRINT",EDGE,{"derivedFrom":sQuery(id+"F26.wireOp",EDGE,"E69.bottom")}),-1.0]])]});
            extrude(context, id + "F27", {"entities" : qUnion([Q0]), "operationType" : NewBodyOperationType.ADD, "depth" : .4 * mm});
        }
        {
            var Q0;
            {var subQ0=sQuery(id+"F0.wireOp",EDGE,"E0.rect.bottom");var subQ1=sQuery(id+"F0.wireOp",EDGE,"E0.rect.top");var subQ2=sQuery(id+"F0.wireOp",EDGE,"E0.rect.left");var subQ3=sQuery(id+"F0.wireOp",EDGE,"E0.rect.right");var subQ4=makeQuery(id+"F1.opExtrude","CAP_FACE",FACE,{"disambiguationData":[OSD([subQ0,subQ1,subQ2,subQ3])],"isStart":true});Q0=makeQuery(id+"F27.boolean.opBoolean","MERGE",FACE,{"derivedFrom":[makeQuery(id+"F25.boolean.opBoolean","MERGE",FACE,{"derivedFrom":[makeQuery(id+"F12.opPattern","COPY",FACE,{"derivedFrom":makeQuery(id+"F11.boolean.opBoolean","SPLIT",FACE,{"disambiguationData":[TD([makeQuery(id+"F1.opExtrude","SWEPT_FACE",FACE,{"disambiguationData":[OSD([subQ3])]})])],"derivedFrom":subQ4}),"instanceName":"1"}),makeQuery(id+"F12.opPattern","COPY",FACE,{"derivedFrom":makeQuery(id+"F11.boolean.opBoolean","SPLIT",FACE,{"disambiguationData":[TD([makeQuery(id+"F1.opExtrude","SWEPT_FACE",FACE,{"disambiguationData":[OSD([subQ2])]})])],"derivedFrom":subQ4}),"instanceName":"1"}),makeQuery(id+"F25.opExtrude","CAP_FACE",FACE,{"disambiguationData":[OSD([sQuery(id+"F24.wireOp",EDGE,"E68.bottom"),sQuery(id+"F24.wireOp",EDGE,"E68.top"),sQuery(id+"F24.wireOp",EDGE,"E68.left"),sQuery(id+"F24.wireOp",EDGE,"E68.right")])],"isStart":false})]}),makeQuery(id+"F27.opExtrude","CAP_FACE",FACE,{"disambiguationData":[OSD([sQuery(id+"F26.wireOp",EDGE,"E69.bottom"),sQuery(id+"F26.wireOp",EDGE,"E69.top"),sQuery(id+"F26.wireOp",EDGE,"E69.left"),sQuery(id+"F26.wireOp",EDGE,"E69.right")])],"isStart":false})]});}
            var sketch = newSketch(context, id + "F28", { "sketchPlane" : qUnion([Q0])});
            skLineSegment(sketch, "E70.bottom", {"start": v(5.82, 20.64) * mm, "end": v(11.12, 20.64) * mm});
            skLineSegment(sketch, "E70.top", {"start": v(5.82, 16.76) * mm, "end": v(11.12, 16.76) * mm});
            skLineSegment(sketch, "E70.left", {"start": v(5.82, 20.64) * mm, "end": v(5.82, 16.76) * mm});
            skLineSegment(sketch, "E70.right", {"start": v(11.12, 20.64) * mm, "end": v(11.12, 16.76) * mm});
            skLineSegment(sketch, "E71.bottom", {"start": v(-6.52, -16.76) * mm, "end": v(-11.82, -16.76) * mm});
            skLineSegment(sketch, "E71.top", {"start": v(-6.52, -20.64) * mm, "end": v(-11.82, -20.64) * mm});
            skLineSegment(sketch, "E71.left", {"start": v(-6.52, -16.76) * mm, "end": v(-6.52, -20.64) * mm});
            skLineSegment(sketch, "E71.right", {"start": v(-11.82, -16.76) * mm, "end": v(-11.82, -20.64) * mm});
            skSolve(sketch);
        }
        {
            var Q0;
            {Q0=qUnion([makeQuery(id+"F28.imprint","IMPRINT",FACE,{"disambiguationData":[TD([[makeQuery(id+"F28.imprint","IMPRINT",EDGE,{"derivedFrom":sQuery(id+"F28.wireOp",EDGE,"E70.bottom")}),1.0]])]}),makeQuery(id+"F28.imprint","IMPRINT",FACE,{"disambiguationData":[TD([[makeQuery(id+"F28.imprint","IMPRINT",EDGE,{"derivedFrom":sQuery(id+"F28.wireOp",EDGE,"E71.bottom")}),1.0]])]})]);}
            extrude(context, id + "F29", {"entities" : qUnion([Q0]), "operationType" : NewBodyOperationType.REMOVE, "oppositeDirection" : true, "depth" : 0.85 * mm});
        }
    });
